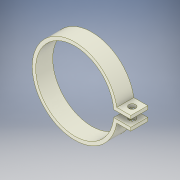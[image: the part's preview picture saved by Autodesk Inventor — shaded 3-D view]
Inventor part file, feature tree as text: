
AUTODESK INVENTOR PART (.ipt)
format: ipt  version: 2019 (Build 230136000, 136)  size: 130,048 bytes
history: native  units: mm
features: extrude x2, sketch x2, projected_geometry x1
ambient origin geometry x8: Origin, YZ Plane, XZ Plane, XY Plane, X Axis, Y Axis, Z Axis, Center Point
bodies: Solid1 (feature_tree)
feature tree (5):
  extrude  "Extrusion1"  Depth=50.0mm
  extrude  "Extrusion2"  Depth=2.0mm
  sketch  "Sketch1"  dims[d0=46.0mm d1=50.0mm]
  sketch  "Sketch2"  dims[d7=2.0mm d9=2.0mm d10=10.0mm d11=0.0mm d12=4.0mm d13=8.5mm d14=0.0mm]
  projected_geometry  "Projected Loop1"
